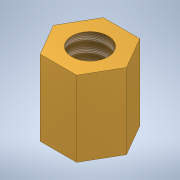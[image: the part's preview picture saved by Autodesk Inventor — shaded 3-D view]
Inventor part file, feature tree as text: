
AUTODESK INVENTOR PART (.ipt)
format: ipt  version: 2022.2 (Build 262287010, 287A)  size: 107,008 bytes
history: native  units: mm
features: sketch x2, extrude x1, hole x1
ambient origin geometry x8: Origin, YZ Plane, XZ Plane, XY Plane, X Axis, Y Axis, Z Axis, Center Point
bodies: Volumenkörper1 (feature_tree)
feature tree (4):
  extrude  "Extrusion1"  Depth=5.5mm TaperAngle=0.0deg
  hole  "Bohrung1"  [1 undecoded]
  sketch  "Skizze1"  dims[d0=4.6mm d1=5.5mm d2=0.0mm]
  sketch  "Skizze2"  dims[d3=2.6416mm d4=7.01mm d5=6.5mm d6=3.4mm d7=14.3117mm d8=8.0mm d9=20.594885mm]
note: 1 required parameter value undecoded (feature->parameter linkage not recoverable at this tier; creation-order binding heuristic only, values carry confidence <= 0.55)
